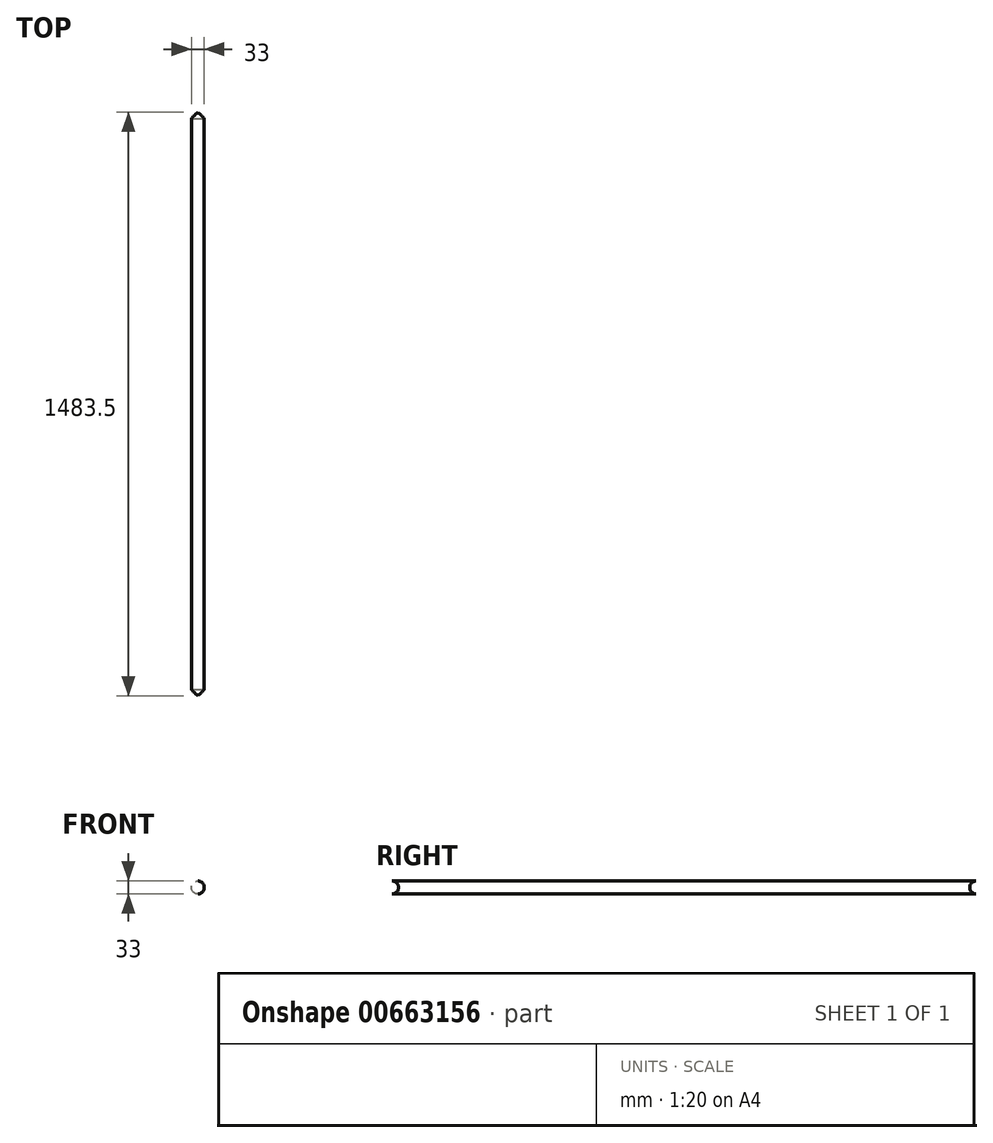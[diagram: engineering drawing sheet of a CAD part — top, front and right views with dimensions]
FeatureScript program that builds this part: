
annotation { "Feature Type Name" : "Feature", "Feature Type Description" : "" }
export const myFeature = defineFeature(function(context is Context, id is Id, definition is map)
    precondition{}
    {
        {
            var Q0;
            Q0=qCreatedBy(makeId("Front.planeOp"),FACE);
            var sketch = newSketch(context, id + "F0", { "sketchPlane" : qUnion([Q0])});
            skLineSegment(sketch, "E0.bottom", {"start": v(16.5, 16.5) * mm, "end": v(-16.5, 16.5) * mm});
            skLineSegment(sketch, "E0.top", {"start": v(16.5, -16.5) * mm, "end": v(-16.5, -16.5) * mm});
            skLineSegment(sketch, "E0.left", {"start": v(16.5, 16.5) * mm, "end": v(16.5, -16.5) * mm});
            skLineSegment(sketch, "E0.right", {"start": v(-16.5, 16.5) * mm, "end": v(-16.5, -16.5) * mm});
            skPoint(sketch, "E0.middle", {"position": v(0, 0) * mm});
            skSolve(sketch);
        }
        {
            var Q0;
            Q0=makeQuery(id+"F0.imprint","IMPRINT",FACE,{"disambiguationData":[TD([[makeQuery(id+"F0.imprint","IMPRINT",EDGE,{"derivedFrom":sQuery(id+"F0.wireOp",EDGE,"E0.bottom")}),1.0]])]});
            extrude(context, id + "F1", {"entities" : qUnion([Q0]), "endBound" : BoundingType.SYMMETRIC, "depth" : 1483.5 * mm, "offsetDistance" : 25 * mm});
        }
        {
            var Q0;
            Q0=makeQuery(id+"F1.opExtrude","SWEPT_FACE",FACE,{"disambiguationData":[OSD([sQuery(id+"F0.wireOp",EDGE,"E0.left")])]});
            var sketch = newSketch(context, id + "F2", { "sketchPlane" : qUnion([Q0])});
            skCircle(sketch, "E1", {"center": v(741.75, 0) * mm, "radius": 16.5 * mm});
            skCircle(sketch, "E2", {"center": v(-741.75, 0) * mm, "radius": 16.5 * mm});
            skSolve(sketch);
        }
        {
            var Q0;
            Q0=makeQuery(id+"F1.opExtrude","SWEPT_EDGE",EDGE,{"disambiguationData":[OSD([sQuery(id+"F0.wireOp",EDGE,"E0.bottom"),sQuery(id+"F0.wireOp",EDGE,"E0.left")])]});
            var Q1;
            Q1=makeQuery(id+"F1.opExtrude","SWEPT_EDGE",EDGE,{"disambiguationData":[OSD([sQuery(id+"F0.wireOp",EDGE,"E0.top"),sQuery(id+"F0.wireOp",EDGE,"E0.left")])]});
            var Q2;
            Q2=makeQuery(id+"F1.opExtrude","SWEPT_EDGE",EDGE,{"disambiguationData":[OSD([sQuery(id+"F0.wireOp",EDGE,"E0.top"),sQuery(id+"F0.wireOp",EDGE,"E0.right")])]});
            var Q3;
            Q3=makeQuery(id+"F1.opExtrude","SWEPT_EDGE",EDGE,{"disambiguationData":[OSD([sQuery(id+"F0.wireOp",EDGE,"E0.bottom"),sQuery(id+"F0.wireOp",EDGE,"E0.right")])]});
            fillet(context, id + "F3", {"entities" : qUnion([Q0, Q1, Q2, Q3]), "radius" : (33 / 2) * mm, "tangentPropagation" : true, "allowEdgeOverflow" : false});
        }
        {
            var Q0;
            {var subQ1=sQuery(id+"F0.wireOp",EDGE,"E0.left");var subQ2=makeQuery(id+"F1.opExtrude","CAP_EDGE",EDGE,{"disambiguationData":[OSD([subQ1])],"isStart":false});Q0=makeQuery(id+"F2.imprint","IMPRINT",FACE,{"disambiguationData":[TD([[makeQuery(id+"F2.imprint","IMPRINT",EDGE,{"derivedFrom":subQ2}),1.0]])]});}
            var Q1;
            {var subQ1=sQuery(id+"F0.wireOp",EDGE,"E0.left");var subQ2=makeQuery(id+"F1.opExtrude","CAP_EDGE",EDGE,{"disambiguationData":[OSD([subQ1])],"isStart":true});Q1=makeQuery(id+"F2.imprint","IMPRINT",FACE,{"disambiguationData":[TD([[makeQuery(id+"F2.imprint","IMPRINT",EDGE,{"derivedFrom":subQ2}),-1.0]])]});}
            extrude(context, id + "F4", {"entities" : qUnion([Q0, Q1]), "operationType" : NewBodyOperationType.REMOVE, "oppositeDirection" : true, "depth" : 50 * mm, "offsetDistance" : 25 * mm});
        }
    });
